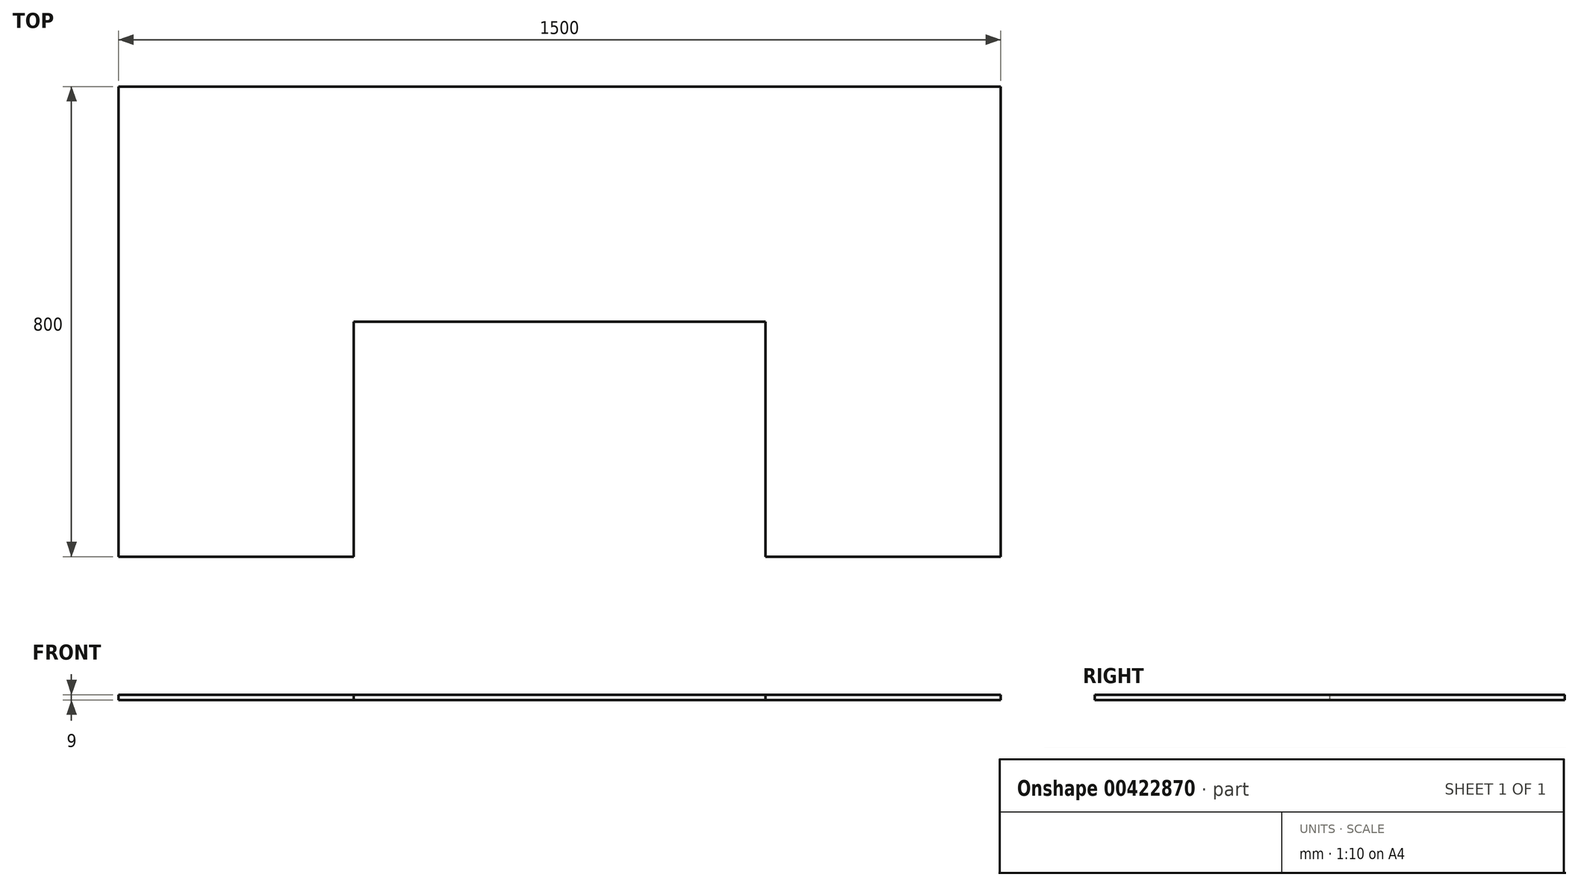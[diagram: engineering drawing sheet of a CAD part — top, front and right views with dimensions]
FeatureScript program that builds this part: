
annotation { "Feature Type Name" : "Feature", "Feature Type Description" : "" }
export const myFeature = defineFeature(function(context is Context, id is Id, definition is map)
    precondition{}
    {
        {
            var Q0;
            Q0=qCreatedBy(makeId("Top.planeOp"),FACE);
            var sketch = newSketch(context, id + "F0", { "sketchPlane" : qUnion([Q0])});
            skLineSegment(sketch, "E0.bottom", {"start": v(-750, 400) * mm, "end": v(750, 400) * mm});
            skLineSegment(sketch, "E0.left", {"start": v(-750, 400) * mm, "end": v(-750, -400) * mm});
            skLineSegment(sketch, "E0.right", {"start": v(750, 400) * mm, "end": v(750, -400) * mm});
            skLineSegment(sketch, "E1", {"start": v(-350, -400) * mm, "end": v(-350, 0) * mm});
            skLineSegment(sketch, "E2", {"start": v(-350, 0) * mm, "end": v(350, 0) * mm});
            skLineSegment(sketch, "E3", {"start": v(350, 0) * mm, "end": v(350, -400) * mm});
            skLineSegment(sketch, "E4", {"start": v(-750, -400) * mm, "end": v(-350, -400) * mm});
            skLineSegment(sketch, "E5", {"start": v(350, -400) * mm, "end": v(750, -400) * mm});
            skSolve(sketch);
        }
        {
            var Q0;
            Q0 = qSketchRegion(id + "F0", true);
            extrude(context, id + "F1", {"entities" : qUnion([Q0]), "endBound" : BoundingType.SYMMETRIC, "depth" : 9 * mm});
        }
    });
